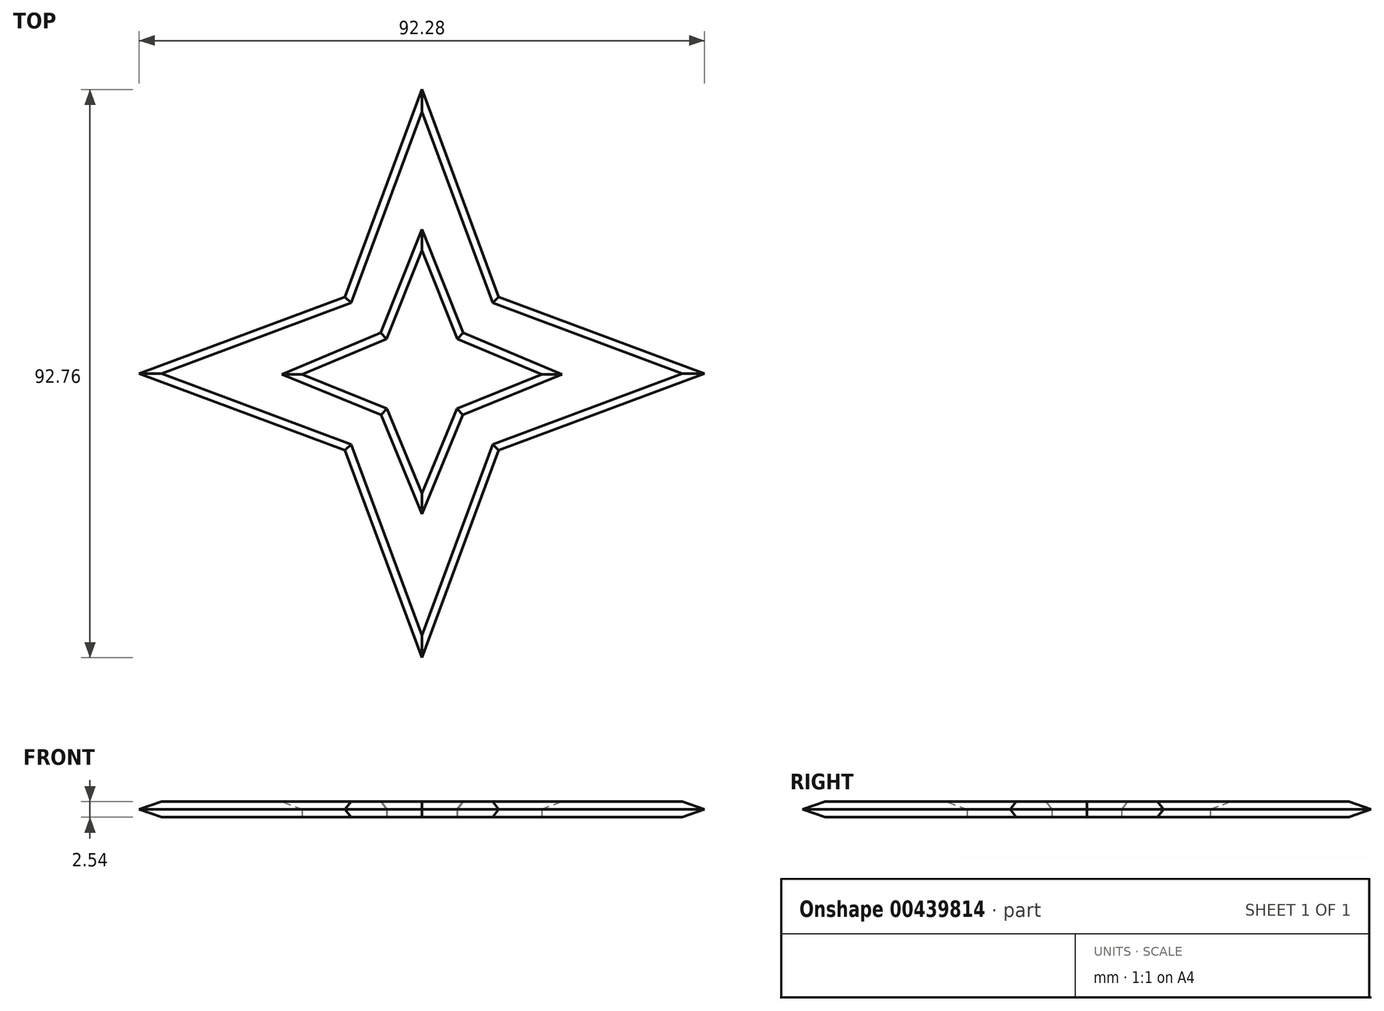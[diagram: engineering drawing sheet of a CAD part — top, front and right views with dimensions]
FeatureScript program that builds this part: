
annotation { "Feature Type Name" : "Feature", "Feature Type Description" : "" }
export const myFeature = defineFeature(function(context is Context, id is Id, definition is map)
    precondition{}
    {
        {
            var Q0;
            Q0=qCreatedBy(makeId("Top.planeOp"),FACE);
            var sketch = newSketch(context, id + "F0", { "sketchPlane" : qUnion([Q0])});
            skPoint(sketch, "E0", {"position": v(0, 46.38) * mm});
            skLineSegment(sketch, "E1", {"start": v(0, 46.38) * mm, "end": v(-12.55, 12.52) * mm});
            skLineSegment(sketch, "E2.MirrorCS", {"start": v(-46.38, -0.1) * mm, "end": v(-12.55, 12.52) * mm});
            skLineSegment(sketch, "E3.MirrorCS", {"start": v(0, 46.38) * mm, "end": v(12.55, 12.52) * mm});
            skLineSegment(sketch, "E4.MirrorCS", {"start": v(46.38, -0.1) * mm, "end": v(12.55, 12.52) * mm});
            skLineSegment(sketch, "E5.MirrorCS", {"start": v(-46.38, 0.1) * mm, "end": v(-12.55, -12.52) * mm});
            skLineSegment(sketch, "E6.MirrorCS", {"start": v(0, -46.38) * mm, "end": v(-12.55, -12.52) * mm});
            skLineSegment(sketch, "E7.MirrorCS", {"start": v(0, -46.38) * mm, "end": v(12.55, -12.52) * mm});
            skLineSegment(sketch, "E8.MirrorCS", {"start": v(46.38, 0.1) * mm, "end": v(12.55, -12.52) * mm});
            skSolve(sketch);
        }
        {
            var Q0;
            Q0=qCreatedBy(makeId("Top.planeOp"),FACE);
            var sketch = newSketch(context, id + "F1", { "sketchPlane" : qUnion([Q0])});
            skLineSegment(sketch, "E9", {"start": v(0, 20.11) * mm, "end": v(5.77, 5.67) * mm});
            skLineSegment(sketch, "E10.MirrorCS", {"start": v(20.11, -0.35) * mm, "end": v(5.77, 5.67) * mm});
            skLineSegment(sketch, "E11.MirrorCS", {"start": v(20.11, 0.12) * mm, "end": v(5.7, -5.73) * mm});
            skLineSegment(sketch, "E12.MirrorCS", {"start": v(-0.23, -20.11) * mm, "end": v(5.7, -5.73) * mm});
            skLineSegment(sketch, "E13.MirrorCS", {"start": v(0, 20.11) * mm, "end": v(-5.77, 5.67) * mm});
            skLineSegment(sketch, "E14.MirrorCS", {"start": v(0.23, -20.11) * mm, "end": v(-5.7, -5.73) * mm});
            skLineSegment(sketch, "E15.MirrorCS", {"start": v(-20.11, 0.12) * mm, "end": v(-5.7, -5.73) * mm});
            skLineSegment(sketch, "E16.MirrorCS", {"start": v(-20.11, -0.35) * mm, "end": v(-5.77, 5.67) * mm});
            skSolve(sketch);
        }
        {
            var Q0;
            Q0 = qSketchRegion(id + "F0", true);
            extrude(context, id + "F2", {"entities" : qUnion([Q0]), "depth" : 2.54 * mm});
        }
        {
            var Q0;
            Q0 = qSketchRegion(id + "F1", true);
            extrude(context, id + "F3", {"entities" : qUnion([Q0]), "operationType" : NewBodyOperationType.REMOVE, "depth" : 23.62 * mm});
        }
        {
            var Q0;
            Q0=makeQuery(id+"F2.opExtrude","CAP_EDGE",EDGE,{"disambiguationData":[OSD([sQuery(id+"F0.wireOp",EDGE,"E7.MirrorCS")])],"isStart":false});
            var Q1;
            Q1=makeQuery(id+"F2.opExtrude","CAP_EDGE",EDGE,{"disambiguationData":[OSD([sQuery(id+"F0.wireOp",EDGE,"E6.MirrorCS")])],"isStart":false});
            var Q2;
            Q2=makeQuery(id+"F2.opExtrude","CAP_EDGE",EDGE,{"disambiguationData":[OSD([sQuery(id+"F0.wireOp",EDGE,"E5.MirrorCS")])],"isStart":false});
            var Q3;
            Q3=makeQuery(id+"F2.opExtrude","CAP_EDGE",EDGE,{"disambiguationData":[OSD([sQuery(id+"F0.wireOp",EDGE,"E2.MirrorCS")])],"isStart":false});
            var Q4;
            Q4=makeQuery(id+"F2.opExtrude","CAP_EDGE",EDGE,{"disambiguationData":[OSD([sQuery(id+"F0.wireOp",EDGE,"E1")])],"isStart":false});
            var Q5;
            Q5=makeQuery(id+"F2.opExtrude","CAP_EDGE",EDGE,{"disambiguationData":[OSD([sQuery(id+"F0.wireOp",EDGE,"E3.MirrorCS")])],"isStart":false});
            var Q6;
            Q6=makeQuery(id+"F2.opExtrude","CAP_EDGE",EDGE,{"disambiguationData":[OSD([sQuery(id+"F0.wireOp",EDGE,"E4.MirrorCS")])],"isStart":false});
            var Q7;
            Q7=makeQuery(id+"F2.opExtrude","CAP_EDGE",EDGE,{"disambiguationData":[OSD([sQuery(id+"F0.wireOp",EDGE,"E8.MirrorCS")])],"isStart":false});
            var Q8;
            Q8=makeQuery(id+"F2.opExtrude","CAP_EDGE",EDGE,{"disambiguationData":[OSD([sQuery(id+"F0.wireOp",EDGE,"E1")])],"isStart":true});
            var Q9;
            Q9=makeQuery(id+"F2.opExtrude","CAP_EDGE",EDGE,{"disambiguationData":[OSD([sQuery(id+"F0.wireOp",EDGE,"E4.MirrorCS")])],"isStart":true});
            var Q10;
            Q10=makeQuery(id+"F2.opExtrude","CAP_EDGE",EDGE,{"disambiguationData":[OSD([sQuery(id+"F0.wireOp",EDGE,"E3.MirrorCS")])],"isStart":true});
            var Q11;
            Q11=makeQuery(id+"F2.opExtrude","CAP_EDGE",EDGE,{"disambiguationData":[OSD([sQuery(id+"F0.wireOp",EDGE,"E8.MirrorCS")])],"isStart":true});
            var Q12;
            Q12=makeQuery(id+"F2.opExtrude","CAP_EDGE",EDGE,{"disambiguationData":[OSD([sQuery(id+"F0.wireOp",EDGE,"E7.MirrorCS")])],"isStart":true});
            var Q13;
            Q13=makeQuery(id+"F2.opExtrude","CAP_EDGE",EDGE,{"disambiguationData":[OSD([sQuery(id+"F0.wireOp",EDGE,"E6.MirrorCS")])],"isStart":true});
            var Q14;
            Q14=makeQuery(id+"F2.opExtrude","CAP_EDGE",EDGE,{"disambiguationData":[OSD([sQuery(id+"F0.wireOp",EDGE,"E5.MirrorCS")])],"isStart":true});
            var Q15;
            Q15=makeQuery(id+"F2.opExtrude","CAP_EDGE",EDGE,{"disambiguationData":[OSD([sQuery(id+"F0.wireOp",EDGE,"E2.MirrorCS")])],"isStart":true});
            var Q16;
            Q16=makeQuery(id+"F3.boolean.opBoolean","COPY",EDGE,{"derivedFrom":makeQuery(id+"F3.opExtrude","CAP_EDGE",EDGE,{"disambiguationData":[OSD([sQuery(id+"F1.wireOp",EDGE,"E16.MirrorCS")])],"isStart":true})});
            var Q17;
            Q17=makeQuery(id+"F2.opExtrude","CAP_FACE",FACE,{"disambiguationData":[OSD([sQuery(id+"F0.wireOp",EDGE,"E1"),sQuery(id+"F0.wireOp",EDGE,"E2.MirrorCS"),sQuery(id+"F0.wireOp",EDGE,"E3.MirrorCS"),sQuery(id+"F0.wireOp",EDGE,"E4.MirrorCS"),sQuery(id+"F0.wireOp",EDGE,"E5.MirrorCS"),sQuery(id+"F0.wireOp",EDGE,"E6.MirrorCS"),sQuery(id+"F0.wireOp",EDGE,"E7.MirrorCS"),sQuery(id+"F0.wireOp",EDGE,"E8.MirrorCS")])],"isStart":false});
            var Q18;
            Q18=makeQuery(id+"F3.boolean.opBoolean","COPY",EDGE,{"derivedFrom":makeQuery(id+"F3.opExtrude","CAP_EDGE",EDGE,{"disambiguationData":[OSD([sQuery(id+"F1.wireOp",EDGE,"E15.MirrorCS")])],"isStart":true})});
            var Q19;
            Q19=makeQuery(id+"F3.boolean.opBoolean","COPY",EDGE,{"derivedFrom":makeQuery(id+"F3.opExtrude","CAP_EDGE",EDGE,{"disambiguationData":[OSD([sQuery(id+"F1.wireOp",EDGE,"E14.MirrorCS")])],"isStart":true})});
            var Q20;
            Q20=makeQuery(id+"F3.boolean.opBoolean","COPY",EDGE,{"derivedFrom":makeQuery(id+"F3.opExtrude","CAP_EDGE",EDGE,{"disambiguationData":[OSD([sQuery(id+"F1.wireOp",EDGE,"E12.MirrorCS")])],"isStart":true})});
            var Q21;
            Q21=makeQuery(id+"F3.boolean.opBoolean","COPY",EDGE,{"derivedFrom":makeQuery(id+"F3.opExtrude","CAP_EDGE",EDGE,{"disambiguationData":[OSD([sQuery(id+"F1.wireOp",EDGE,"E11.MirrorCS")])],"isStart":true})});
            var Q22;
            Q22=makeQuery(id+"F3.boolean.opBoolean","COPY",EDGE,{"derivedFrom":makeQuery(id+"F3.opExtrude","CAP_EDGE",EDGE,{"disambiguationData":[OSD([sQuery(id+"F1.wireOp",EDGE,"E10.MirrorCS")])],"isStart":true})});
            var Q23;
            Q23=makeQuery(id+"F3.boolean.opBoolean","COPY",EDGE,{"derivedFrom":makeQuery(id+"F3.opExtrude","CAP_EDGE",EDGE,{"disambiguationData":[OSD([sQuery(id+"F1.wireOp",EDGE,"E9")])],"isStart":true})});
            var Q24;
            Q24=makeQuery(id+"F3.boolean.opBoolean","COPY",EDGE,{"derivedFrom":makeQuery(id+"F3.opExtrude","CAP_EDGE",EDGE,{"disambiguationData":[OSD([sQuery(id+"F1.wireOp",EDGE,"E13.MirrorCS")])],"isStart":true})});
            chamfer(context, id + "F4", {"entities" : qUnion([Q0, Q1, Q2, Q3, Q4, Q5, Q6, Q7, Q8, Q9, Q10, Q11, Q12, Q13, Q14, Q15, Q16, Q17, Q18, Q19, Q20, Q21, Q22, Q23, Q24]), "width" : 1.27 * mm, "tangentPropagation" : true});
        }
    });
